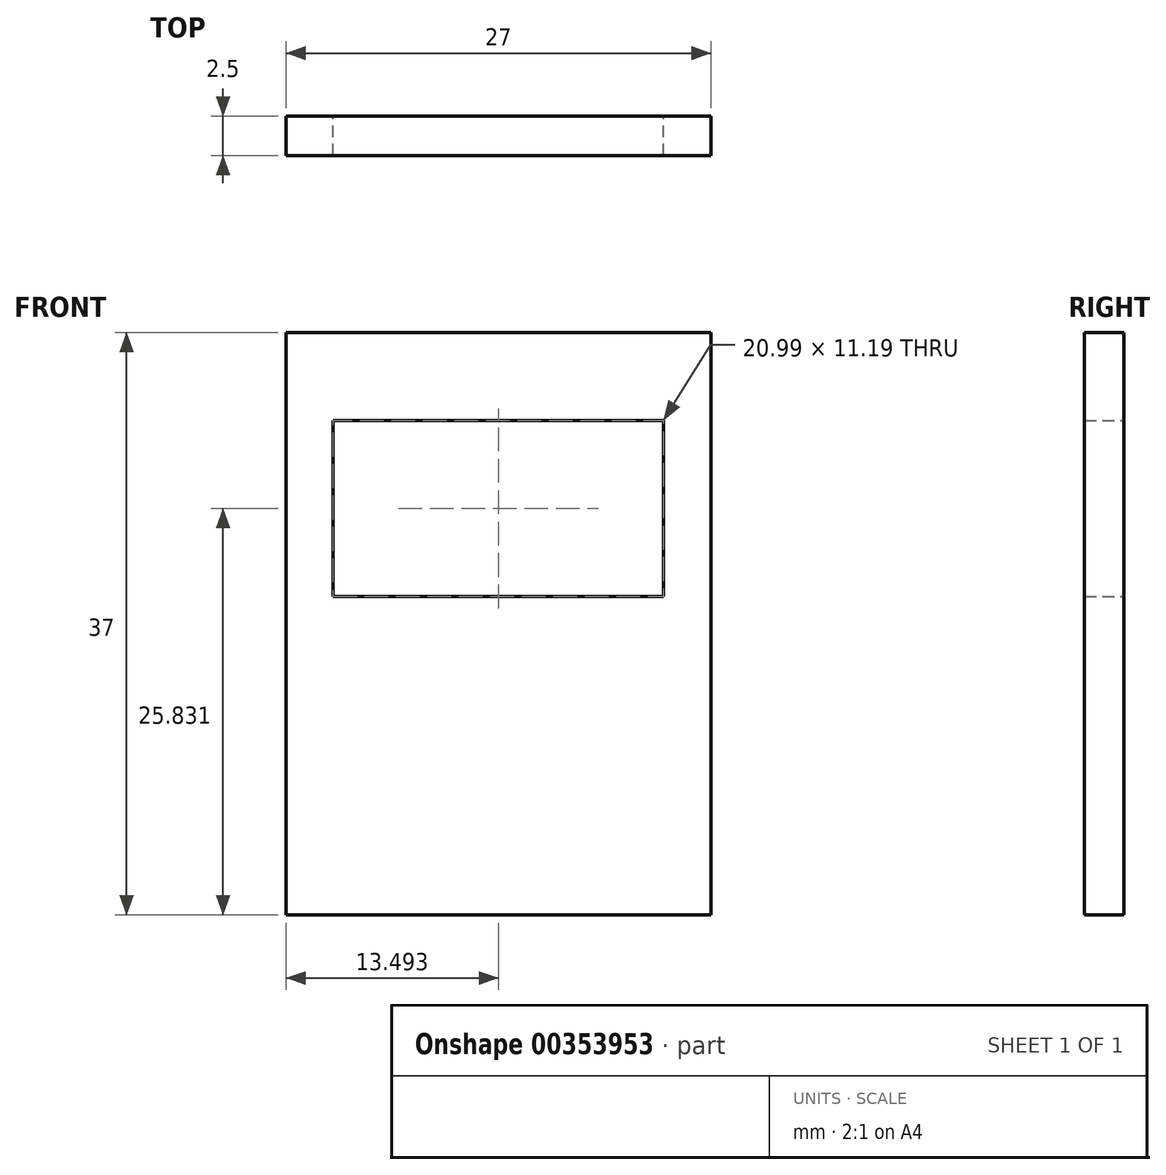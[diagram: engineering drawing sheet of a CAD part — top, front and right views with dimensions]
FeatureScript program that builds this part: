
annotation { "Feature Type Name" : "Feature", "Feature Type Description" : "" }
export const myFeature = defineFeature(function(context is Context, id is Id, definition is map)
    precondition{}
    {
        {
            var Q0;
            Q0=qCreatedBy(makeId("Front.planeOp"),FACE);
            var sketch = newSketch(context, id + "F0", { "sketchPlane" : qUnion([Q0])});
            skLineSegment(sketch, "E0", {"start": v(40.19, 24.76) * mm, "end": v(40.19, -12.24) * mm});
            skLineSegment(sketch, "E1", {"start": v(40.19, -12.24) * mm, "end": v(13.19, -12.24) * mm});
            skLineSegment(sketch, "E2", {"start": v(13.19, -12.24) * mm, "end": v(13.19, 24.76) * mm});
            skLineSegment(sketch, "E3", {"start": v(13.19, 24.76) * mm, "end": v(40.19, 24.76) * mm});
            skLineSegment(sketch, "E4.bottom", {"start": v(37.18, 19.19) * mm, "end": v(16.19, 19.19) * mm});
            skLineSegment(sketch, "E4.top", {"start": v(37.18, 8) * mm, "end": v(16.19, 8) * mm});
            skLineSegment(sketch, "E4.left", {"start": v(37.18, 19.19) * mm, "end": v(37.18, 8) * mm});
            skLineSegment(sketch, "E4.right", {"start": v(16.19, 19.19) * mm, "end": v(16.19, 8) * mm});
            skSolve(sketch);
        }
        {
            var Q0;
            Q0=makeQuery(id+"F0.imprint","IMPRINT",FACE,{"disambiguationData":[TD([[makeQuery(id+"F0.imprint","IMPRINT",EDGE,{"derivedFrom":sQuery(id+"F0.wireOp",EDGE,"E0")}),-1.0]])]});
            extrude(context, id + "F1", {"entities" : qUnion([Q0]), "depth" : 2.5 * mm});
        }
    });
